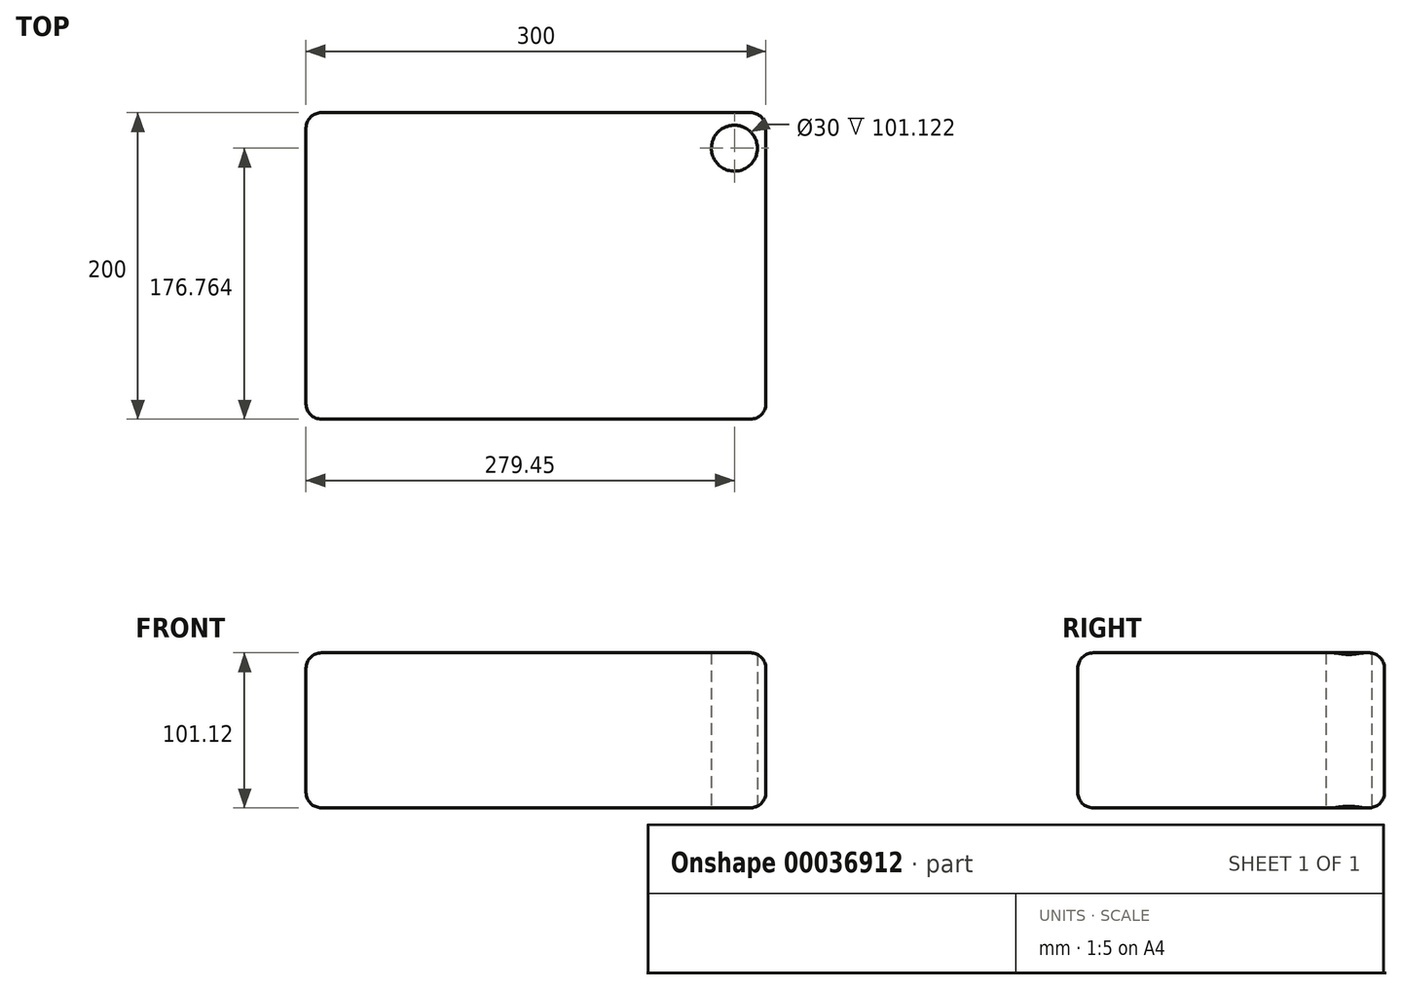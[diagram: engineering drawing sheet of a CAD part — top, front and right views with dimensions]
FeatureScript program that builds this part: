
annotation { "Feature Type Name" : "Feature", "Feature Type Description" : "" }
export const myFeature = defineFeature(function(context is Context, id is Id, definition is map)
    precondition{}
    {
        {
            var Q0;
            Q0=qCreatedBy(makeId("Top.planeOp"),FACE);
            var sketch = newSketch(context, id + "F0", { "sketchPlane" : qUnion([Q0])});
            skLineSegment(sketch, "E0.bottom", {"start": v(-149.93, 130.1) * mm, "end": v(150.07, 130.1) * mm});
            skLineSegment(sketch, "E0.top", {"start": v(-149.93, -69.9) * mm, "end": v(150.07, -69.9) * mm});
            skLineSegment(sketch, "E0.left", {"start": v(-149.93, 130.1) * mm, "end": v(-149.93, -69.9) * mm});
            skLineSegment(sketch, "E0.right", {"start": v(150.07, 130.1) * mm, "end": v(150.07, -69.9) * mm});
            skCircle(sketch, "E1", {"center": v(129.52, 106.87) * mm, "radius": 15 * mm});
            skSolve(sketch);
        }
        {
            var Q0;
            Q0=makeQuery(id+"F0.imprint","IMPRINT",FACE,{"disambiguationData":[TD([[makeQuery(id+"F0.imprint","IMPRINT",EDGE,{"derivedFrom":sQuery(id+"F0.wireOp",EDGE,"E0.bottom")}),-1.0]])]});
            extrude(context, id + "F1", {"entities" : qUnion([Q0]), "depth" : 101.12 * mm});
        }
        {
            var Q0;
            Q0=makeQuery(id+"F1.opExtrude","SWEPT_EDGE",EDGE,{"disambiguationData":[OSD([sQuery(id+"F0.wireOp",EDGE,"E0.bottom"),sQuery(id+"F0.wireOp",EDGE,"E0.left")])]});
            var Q1;
            Q1=makeQuery(id+"F1.opExtrude","SWEPT_FACE",FACE,{"disambiguationData":[OSD([sQuery(id+"F0.wireOp",EDGE,"E0.bottom")])]});
            var Q2;
            Q2=makeQuery(id+"F1.opExtrude","CAP_EDGE",EDGE,{"disambiguationData":[OSD([sQuery(id+"F0.wireOp",EDGE,"E0.bottom")])],"isStart":false});
            var Q3;
            Q3=makeQuery(id+"F1.opExtrude","CAP_EDGE",EDGE,{"disambiguationData":[OSD([sQuery(id+"F0.wireOp",EDGE,"E0.bottom")])],"isStart":true});
            var Q4;
            Q4=makeQuery(id+"F1.opExtrude","SWEPT_EDGE",EDGE,{"disambiguationData":[OSD([sQuery(id+"F0.wireOp",EDGE,"E0.bottom"),sQuery(id+"F0.wireOp",EDGE,"E0.right")])]});
            fillet(context, id + "F2", {"entities" : qUnion([Q0, Q1, Q2, Q3, Q4]), "radius" : 10 * mm, "tangentPropagation" : true, "allowEdgeOverflow" : false});
        }
        {
            var Q0;
            Q0=makeQuery(id+"F1.opExtrude","CAP_EDGE",EDGE,{"disambiguationData":[OSD([sQuery(id+"F0.wireOp",EDGE,"E0.left")])],"isStart":true});
            var Q1;
            Q1=makeQuery(id+"F1.opExtrude","CAP_EDGE",EDGE,{"disambiguationData":[OSD([sQuery(id+"F0.wireOp",EDGE,"E0.top")])],"isStart":true});
            var Q2;
            Q2=makeQuery(id+"F1.opExtrude","SWEPT_EDGE",EDGE,{"disambiguationData":[OSD([sQuery(id+"F0.wireOp",EDGE,"E0.top"),sQuery(id+"F0.wireOp",EDGE,"E0.left")])]});
            var Q3;
            Q3=makeQuery(id+"F1.opExtrude","CAP_EDGE",EDGE,{"disambiguationData":[OSD([sQuery(id+"F0.wireOp",EDGE,"E0.top")])],"isStart":false});
            var Q4;
            {var subQ0=sQuery(id+"F0.wireOp",EDGE,"E0.bottom");Q4=makeQuery(id+"F2.opFillet","BLEND_EDGE",EDGE,{"disambiguationData":[OD(0.0)],"blendedFrom":[makeQuery(id+"F1.opExtrude","CAP_EDGE",EDGE,{"disambiguationData":[OSD([subQ0])],"isStart":true}),makeQuery(id+"F1.opExtrude","CAP_FACE",FACE,{"disambiguationData":[OSD([subQ0,sQuery(id+"F0.wireOp",EDGE,"E0.top"),sQuery(id+"F0.wireOp",EDGE,"E0.left"),sQuery(id+"F0.wireOp",EDGE,"E0.right"),sQuery(id+"F0.wireOp",EDGE,"E1")])],"isStart":true})],"blendedInto":[makeQuery(id+"F1.opExtrude","CAP_FACE",FACE,{"disambiguationData":[OSD([subQ0,sQuery(id+"F0.wireOp",EDGE,"E0.top"),sQuery(id+"F0.wireOp",EDGE,"E0.left"),sQuery(id+"F0.wireOp",EDGE,"E0.right"),sQuery(id+"F0.wireOp",EDGE,"E1")])],"isStart":true})]});}
            var Q5;
            Q5=makeQuery(id+"F1.opExtrude","CAP_EDGE",EDGE,{"disambiguationData":[OSD([sQuery(id+"F0.wireOp",EDGE,"E0.right")])],"isStart":true});
            var Q6;
            {var subQ0=sQuery(id+"F0.wireOp",EDGE,"E0.bottom");Q6=makeQuery(id+"F2.opFillet","BLEND_EDGE",EDGE,{"disambiguationData":[OD(1.0)],"blendedFrom":[makeQuery(id+"F1.opExtrude","CAP_EDGE",EDGE,{"disambiguationData":[OSD([subQ0])],"isStart":true}),makeQuery(id+"F1.opExtrude","CAP_FACE",FACE,{"disambiguationData":[OSD([subQ0,sQuery(id+"F0.wireOp",EDGE,"E0.top"),sQuery(id+"F0.wireOp",EDGE,"E0.left"),sQuery(id+"F0.wireOp",EDGE,"E0.right"),sQuery(id+"F0.wireOp",EDGE,"E1")])],"isStart":true})],"blendedInto":[makeQuery(id+"F1.opExtrude","CAP_FACE",FACE,{"disambiguationData":[OSD([subQ0,sQuery(id+"F0.wireOp",EDGE,"E0.top"),sQuery(id+"F0.wireOp",EDGE,"E0.left"),sQuery(id+"F0.wireOp",EDGE,"E0.right"),sQuery(id+"F0.wireOp",EDGE,"E1")])],"isStart":true})]});}
            var Q7;
            Q7=makeQuery(id+"F1.opExtrude","SWEPT_EDGE",EDGE,{"disambiguationData":[OSD([sQuery(id+"F0.wireOp",EDGE,"E0.top"),sQuery(id+"F0.wireOp",EDGE,"E0.right")])]});
            var Q8;
            Q8=makeQuery(id+"F1.opExtrude","CAP_EDGE",EDGE,{"disambiguationData":[OSD([sQuery(id+"F0.wireOp",EDGE,"E0.right")])],"isStart":false});
            var Q9;
            {var subQ0=sQuery(id+"F0.wireOp",EDGE,"E0.right");Q9=makeQuery(id+"F2.opFillet","BLEND_EDGE",EDGE,{"blendedFrom":[makeQuery(id+"F1.opExtrude","SWEPT_EDGE",EDGE,{"disambiguationData":[OSD([sQuery(id+"F0.wireOp",EDGE,"E0.bottom"),subQ0])]}),makeQuery(id+"F1.opExtrude","SWEPT_FACE",FACE,{"disambiguationData":[OSD([subQ0])]})],"blendedInto":[makeQuery(id+"F1.opExtrude","SWEPT_FACE",FACE,{"disambiguationData":[OSD([subQ0])]})]});}
            var Q10;
            {var subQ0=sQuery(id+"F0.wireOp",EDGE,"E0.bottom");Q10=makeQuery(id+"F2.opFillet","BLEND_EDGE",EDGE,{"disambiguationData":[OD(0.0)],"blendedFrom":[makeQuery(id+"F1.opExtrude","CAP_EDGE",EDGE,{"disambiguationData":[OSD([subQ0])],"isStart":false}),makeQuery(id+"F1.opExtrude","CAP_FACE",FACE,{"disambiguationData":[OSD([subQ0,sQuery(id+"F0.wireOp",EDGE,"E0.top"),sQuery(id+"F0.wireOp",EDGE,"E0.left"),sQuery(id+"F0.wireOp",EDGE,"E0.right"),sQuery(id+"F0.wireOp",EDGE,"E1")])],"isStart":false})],"blendedInto":[makeQuery(id+"F1.opExtrude","CAP_FACE",FACE,{"disambiguationData":[OSD([subQ0,sQuery(id+"F0.wireOp",EDGE,"E0.top"),sQuery(id+"F0.wireOp",EDGE,"E0.left"),sQuery(id+"F0.wireOp",EDGE,"E0.right"),sQuery(id+"F0.wireOp",EDGE,"E1")])],"isStart":false})]});}
            var Q11;
            {var subQ0=sQuery(id+"F0.wireOp",EDGE,"E0.bottom");Q11=makeQuery(id+"F2.opFillet","BLEND_EDGE",EDGE,{"disambiguationData":[OD(1.0)],"blendedFrom":[makeQuery(id+"F1.opExtrude","CAP_EDGE",EDGE,{"disambiguationData":[OSD([subQ0])],"isStart":false}),makeQuery(id+"F1.opExtrude","CAP_FACE",FACE,{"disambiguationData":[OSD([subQ0,sQuery(id+"F0.wireOp",EDGE,"E0.top"),sQuery(id+"F0.wireOp",EDGE,"E0.left"),sQuery(id+"F0.wireOp",EDGE,"E0.right"),sQuery(id+"F0.wireOp",EDGE,"E1")])],"isStart":false})],"blendedInto":[makeQuery(id+"F1.opExtrude","CAP_FACE",FACE,{"disambiguationData":[OSD([subQ0,sQuery(id+"F0.wireOp",EDGE,"E0.top"),sQuery(id+"F0.wireOp",EDGE,"E0.left"),sQuery(id+"F0.wireOp",EDGE,"E0.right"),sQuery(id+"F0.wireOp",EDGE,"E1")])],"isStart":false})]});}
            var Q12;
            Q12=makeQuery(id+"F1.opExtrude","CAP_EDGE",EDGE,{"disambiguationData":[OSD([sQuery(id+"F0.wireOp",EDGE,"E0.left")])],"isStart":false});
            fillet(context, id + "F3", {"entities" : qUnion([Q0, Q1, Q2, Q3, Q4, Q5, Q6, Q7, Q8, Q9, Q10, Q11, Q12]), "radius" : 10 * mm, "tangentPropagation" : true, "allowEdgeOverflow" : false});
        }
    });
